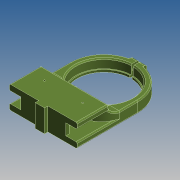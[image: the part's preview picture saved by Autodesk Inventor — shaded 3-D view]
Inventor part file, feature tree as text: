
AUTODESK INVENTOR PART (.ipt)
format: ipt  version: 2015 SP1 (Build 190203100, 203)  size: 680,448 bytes
history: native  units: mm
features: sketch x15, fillet x10, extrude x9, hole x6, projected_geometry x6, mirror x4, other x2, chamfer x1
ambient origin geometry x8: Origin, YZ Plane, XZ Plane, XY Plane, X Axis, Y Axis, Z Axis, Center Point
bodies: Solid2 (feature_tree)
feature tree (53):
  extrude  "Extrusion2"  Depth=20.0mm
  extrude  "Extrusion3"  Depth=10.0mm TaperAngle=0.0deg
  hole  "Trou pour ressort"  [1 undecoded]
  mirror  "Mirror1"
  extrude  "Extrusion5"  Depth=30.0mm
  extrude  "Extrusion6"  Depth=2.0mm TaperAngle=0.0deg
  hole  "Hole4"  [1 undecoded]
  fillet  "Fillet3"  Radius=60.0mm
  fillet  "Fillet4"  Radius=30.0mm
  hole  "Hole5"  [1 undecoded]
  extrude  "Extrusion12"  Depth=2.0mm
  extrude  "Extrusion13"  TaperAngle=0.0deg  [1 undecoded]
  fillet  "Fillet15"  Radius=1.0mm
  hole  "Hole9"  [1 undecoded]
  extrude  "Extrusion14"  Depth=1.0mm
  mirror  "Mirror3"
  other  "Work Axis1"
  hole  "Hole10"  [1 undecoded]
  fillet  "Fillet16"  Radius=1.0mm
  fillet  "Fillet17"  Radius=1.0mm
  fillet  "Fillet18"  Radius=3.0mm
  chamfer  "Chamfer2"  Distance=5.5mm
  fillet  "Fillet19"  Radius=3.0mm
  fillet  "Fillet22"  Radius=28.0mm
  fillet  "Fillet23"  Radius=4.0mm
  fillet  "Fillet24"  Radius=10.0mm
  extrude  "Extrusion16"  Depth=5.0mm
  other  "Work Axis2"
  hole  "Hole12"  [1 undecoded]
  mirror  "Mirror4"
  extrude  "Extrusion17"  Depth=20.0mm
  mirror  "Mirror5"
  sketch  "Sketch1"  dims[d14=20.0mm d15=20.0mm d16=0.0mm d19=3.0mm]
  sketch  "Sketch3"  dims[d20=5.0mm d21=10.0mm d22=0.0mm]
  sketch  "Sketch6"  dims[d42=22.0mm d43=4.1mm]
  sketch  "Sketch8"  dims[d44=30.0mm d45=3.0mm]
  sketch  "Sketch9"  dims[d49=4.0mm]
  sketch  "Sketch10"  dims[d50=5.0mm d51=6.0mm d52=4.0mm d53=2.0mm d54=90.0deg d55=8.0mm d56=20.594885mm d60=2.0mm d61=0.0mm]
  sketch  "Sketch12"  dims[d62=3.0mm d66=16.0mm d67=60.0mm d68=0.0mm d69=30.0mm]
  sketch  "Sketch21"  dims[d70=48.0mm d71=6.0mm d72=50.0mm d73=18.0mm d74=90.0deg d75=8.0mm d76=20.594885mm d77=30.0mm]
  sketch  "Sketch22"  dims[d78=11.5mm]
  sketch  "Sketch23"  dims[d79=6.0mm d80=6.0mm d81=4.0mm d82=2.0mm d83=90.0deg d84=8.0mm d85=20.594885mm d141=35.0mm]
  sketch  "Sketch24"  dims[d142=2.0mm d143=0.0mm d144=0.0mm d145=1.0mm]
  sketch  "Sketch25"  dims[d146=10.0mm d147=10.0mm d148=0.0mm]
  sketch  "Sketch28"  dims[d149=10.0mm]
  sketch  "Sketch29"  dims[d150=52.0mm d151=6.0mm d152=4.0mm d153=2.0mm d154=90.0deg d155=10.0mm d156=0.0mm d157=1.0mm]
  projected_geometry  "Projected Loop2"
  sketch  "Sketch30"  dims[d158=1.0mm d159=1.0mm d160=1.0mm d161=2.0mm d162=45.0deg d163=1.0mm d164=3.0mm d165=5.5mm d166=3.0mm d167=28.0mm d170=4.0mm d171=10.0mm d172=0.0mm d173=5.0mm d174=28.0mm d175=3.3mm d176=6.0mm d177=6.0mm d178=24.0mm d179=90.0deg d180=10.0mm d181=0.0mm d196=6.0mm d199=1.0mm d200=1.0mm d201=2.0mm d202=5.5mm d203=10.0mm d204=0.0mm d205=3.0mm d206=1.5mm d207=6.0mm d208=4.0mm d209=2.0mm d210=90.0deg d211=2.0mm d212=20.594885mm d213=6.0mm d214=3.0mm d215=2.5mm d216=5.0mm d217=83.0mm d218=0.0mm d219=20.0mm d220=17.0mm]
  projected_geometry  "Project Cut Edges2"
  projected_geometry  "Project Cut Edges4"
  projected_geometry  "Project Cut Edges5"
  projected_geometry  "Project Cut Edges7"
  projected_geometry  "Project Cut Edges8"
note: 7 required parameter values undecoded (feature->parameter linkage not recoverable at this tier; creation-order binding heuristic only, values carry confidence <= 0.55)
